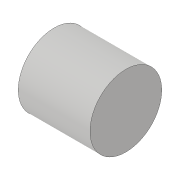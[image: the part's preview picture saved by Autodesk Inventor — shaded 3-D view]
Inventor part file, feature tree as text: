
AUTODESK INVENTOR PART (.ipt)
format: ipt  version: 2019 (Build 230136000, 136)  size: 81,920 bytes
history: native  units: in
note: dims shown in document units (in); Inventor stores cm internally (conversion verified against a paired STEP export)
features: extrude x1, sketch x1
ambient origin geometry x8: Origin, YZ Plane, XZ Plane, XY Plane, X Axis, Y Axis, Z Axis, Center Point
bodies: Solid1 (feature_tree)
feature tree (2):
  extrude  "Extrusion1"  Depth=7.874in TaperAngle=0.0deg
  sketch  "Sketch1"  dims[d0=7.874in d1=7.874in d2=0.0in]
